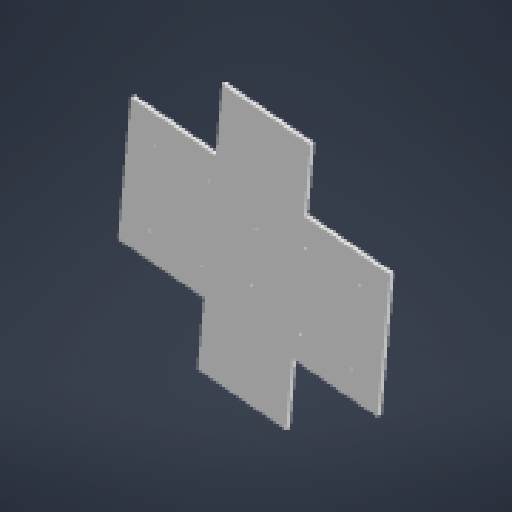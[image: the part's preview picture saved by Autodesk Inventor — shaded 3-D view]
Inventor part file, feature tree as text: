
AUTODESK INVENTOR PART (.ipt)
format: ipt  version: 2024.2 (Build 282272000, 272)  size: 153,600 bytes
history: native  units: in
note: dims shown in document units (in); Inventor stores cm internally (conversion verified against a paired STEP export)
features: reference x18, other x10, sketch x1, plane x1, extrude x1
ambient origin geometry x8: Origin, YZ Plane, XZ Plane, XY Plane, X Axis, Y Axis, Z Axis, Center Point
bodies: Solid1 (feature_tree)
feature tree (31):
  sketch  "Sketch1"  dims[d0=0.126in d1=0.126in d2=0.126in d3=0.126in d4=0.126in d5=0.126in d6=0.126in d7=0.126in d8=0.144in d9=0.144in d10=1.0in d11=0.0in]
  plane  "Work Plane1"
  extrude  "Extrusion1"  Depth=0.126in
  reference  "Reference1"
  reference  "Reference2"
  reference  "Reference3"
  reference  "Reference4"
  reference  "Reference5"
  reference  "Reference6"
  reference  "Reference7"
  reference  "Reference8"
  reference  "Reference9"
  reference  "Reference10"
  reference  "Reference11"
  reference  "Reference12"
  reference  "Reference13"
  reference  "Reference14"
  reference  "Reference15"
  reference  "Reference16"
  reference  "Reference17"
  reference  "Reference18"
  other  "Assembly1"
  other  "Pod_pre_mirror:1"
  other  "Pod_pre_mirror_Top_Right:1"
  other  "Pod_pre_mirror_Bottom_Left:1"
  other  "Pod:1"
  other  "Lower_Plate:1"
  other  "REV Robotics Expansion Hub REV-31-1153 - Expansion Hub:1"
  other  "Servo Power Module REV-11-1144 - Servo Power Module REV-11-1144:1"
  other  "top_shell"
  other  "Control Hub REV-31-1152 - Control Hub REV-31-1152:1"
